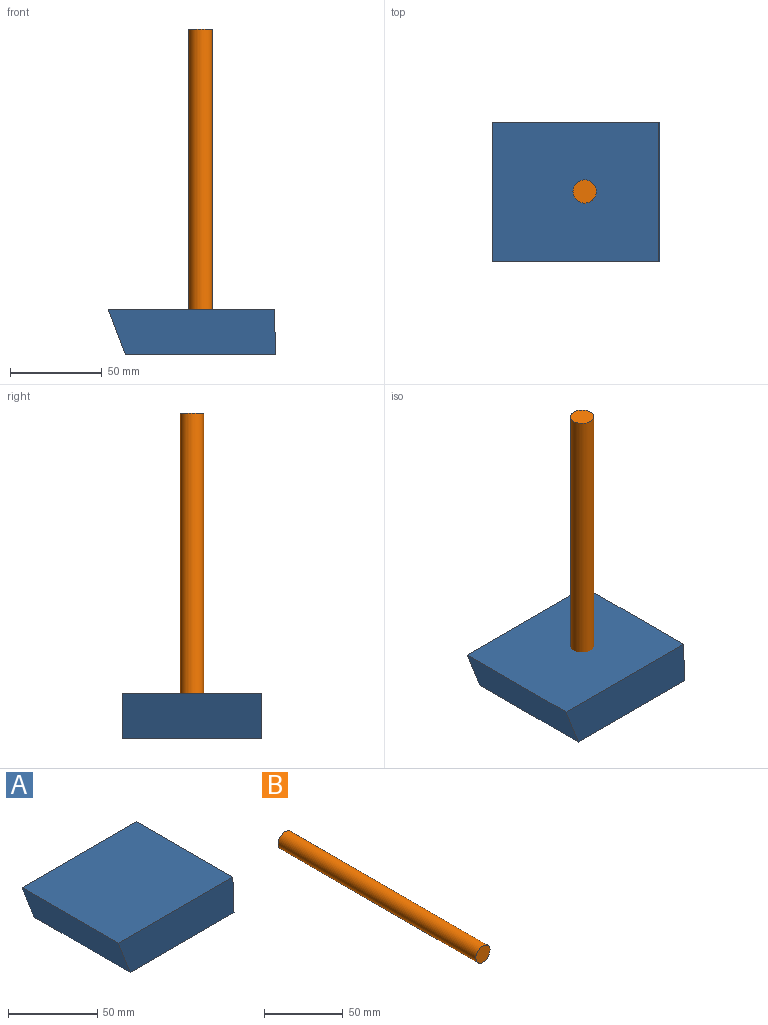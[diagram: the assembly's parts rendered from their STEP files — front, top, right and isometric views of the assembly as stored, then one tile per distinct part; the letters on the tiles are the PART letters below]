
ASSEMBLY  parts=2 mates=1
PART A: 6 faces, bbox 91.5x76.2x24.7 mm
  f0: plane 76.2x24.73mm, normal (1,0,0.04), area 1885.9mm2, adj f1,f3,f4,f5
  f1: plane 90.58x76.2mm, normal (0,0,1), area 6901.8mm2, adj f0,f2,f4,f5
  f2: plane 76.2x24.73mm, normal (-0.93,0,-0.36), area 2016.5mm2, adj f1,f3,f4,f5
  f3: plane 82.06x76.2mm, normal (0,0,-1), area 6253.2mm2, adj f0,f2,f4,f5
  f4: plane 91.47x24.73mm, normal (0,-1,0), area 2135mm2, adj f0,f1,f2,f3
  f5: plane 91.47x24.73mm, normal (0,1,0), area 2135mm2, adj f0,f1,f2,f3
PART B: 3 faces, bbox 12.7x177.8x12.7 mm
  f0: cylinder r=6.35mm len=177.8mm, axis (0,1,0), area 7093.9mm2, adj f1,f2
  f1: plane 12.7x12.7mm, normal (0,-1,0), area 126.7mm2, adj f0
  f2: plane 12.7x12.7mm, normal (0,1,0), area 126.7mm2, adj f0
PLACE A t=(-6.59,7.55,-3.12)mm
PLACE B rot(axis=(0.58,0.58,0.58),120deg) t=(6.49,-30.55,118.06)mm
MATE fastened B.f0 <-> A.f3  axis (0,0,-1) through (6.49,-30.55,-59.74)mm
